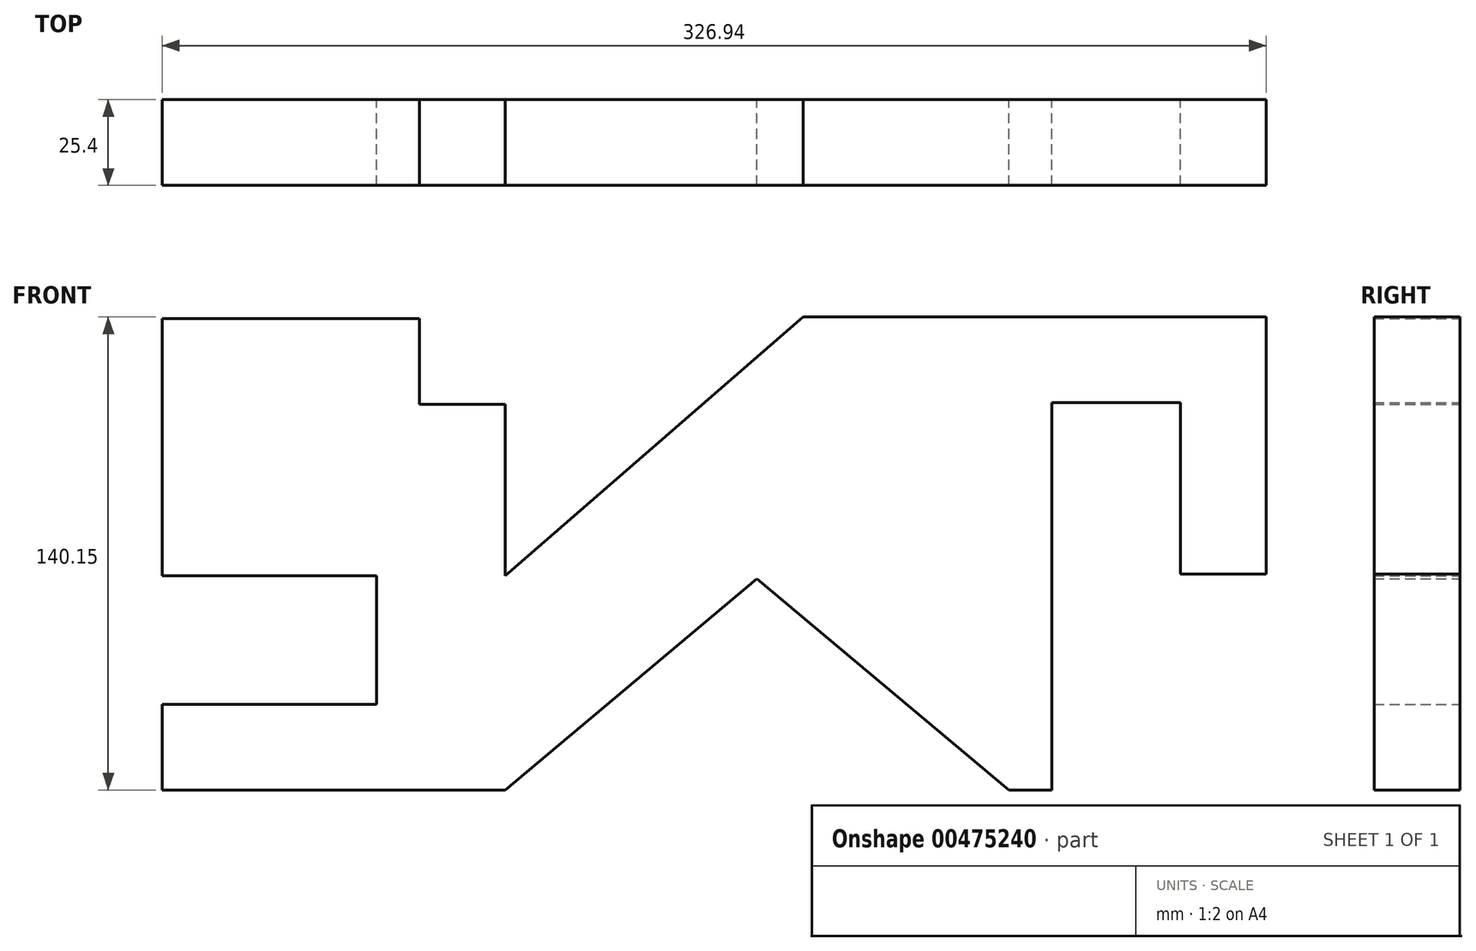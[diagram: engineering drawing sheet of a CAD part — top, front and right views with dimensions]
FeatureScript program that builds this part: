
annotation { "Feature Type Name" : "Feature", "Feature Type Description" : "" }
export const myFeature = defineFeature(function(context is Context, id is Id, definition is map)
    precondition{}
    {
        {
            var Q0;
            Q0=qCreatedBy(makeId("Front.planeOp"),FACE);
            var sketch = newSketch(context, id + "F0", { "sketchPlane" : qUnion([Q0])});
            skLineSegment(sketch, "E0", {"start": v(0, 0) * mm, "end": v(0, -76.2) * mm});
            skLineSegment(sketch, "E1", {"start": v(0, -76.2) * mm, "end": v(63.5, -76.2) * mm});
            skLineSegment(sketch, "E2", {"start": v(63.5, -76.2) * mm, "end": v(63.5, -114.3) * mm});
            skLineSegment(sketch, "E3", {"start": v(63.5, -114.3) * mm, "end": v(0, -114.3) * mm});
            skLineSegment(sketch, "E4", {"start": v(0, -114.3) * mm, "end": v(0, -139.7) * mm});
            skLineSegment(sketch, "E5", {"start": v(0, -139.7) * mm, "end": v(101.6, -139.7) * mm});
            skLineSegment(sketch, "E6", {"start": v(0, 0) * mm, "end": v(76.2, 0) * mm});
            skLineSegment(sketch, "E7", {"start": v(76.2, 0) * mm, "end": v(76.2, -25.4) * mm});
            skLineSegment(sketch, "E8", {"start": v(76.2, -25.4) * mm, "end": v(101.6, -25.4) * mm});
            skLineSegment(sketch, "E9", {"start": v(101.6, -25.4) * mm, "end": v(101.6, -76.2) * mm});
            skLineSegment(sketch, "E10", {"start": v(101.6, -76.2) * mm, "end": v(189.78, 0.45) * mm});
            skLineSegment(sketch, "E11", {"start": v(189.78, 0.45) * mm, "end": v(326.94, 0.45) * mm});
            skLineSegment(sketch, "E12", {"start": v(326.94, 0.45) * mm, "end": v(326.94, -75.75) * mm});
            skLineSegment(sketch, "E13", {"start": v(326.94, -75.75) * mm, "end": v(301.54, -75.75) * mm});
            skLineSegment(sketch, "E14", {"start": v(301.54, -75.75) * mm, "end": v(301.54, -24.95) * mm});
            skLineSegment(sketch, "E15", {"start": v(301.54, -24.95) * mm, "end": v(263.44, -24.95) * mm});
            skLineSegment(sketch, "E16", {"start": v(263.44, -24.95) * mm, "end": v(263.44, -139.7) * mm});
            skLineSegment(sketch, "E17", {"start": v(263.44, -139.7) * mm, "end": v(250.74, -139.7) * mm});
            skLineSegment(sketch, "E18", {"start": v(250.74, -139.7) * mm, "end": v(176.17, -77.13) * mm});
            skLineSegment(sketch, "E19", {"start": v(176.17, -77.13) * mm, "end": v(101.6, -139.7) * mm});
            skSolve(sketch);
        }
        {
            var Q0;
            Q0=makeQuery(id+"F0.imprint","IMPRINT",FACE,{"disambiguationData":[TD([[makeQuery(id+"F0.imprint","IMPRINT",EDGE,{"derivedFrom":sQuery(id+"F0.wireOp",EDGE,"E0")}),1.0]])]});
            extrude(context, id + "F1", {"entities" : qUnion([Q0]), "depth" : 25.4 * mm});
        }
    });
